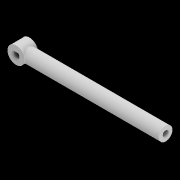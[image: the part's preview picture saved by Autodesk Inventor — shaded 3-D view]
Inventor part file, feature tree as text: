
AUTODESK INVENTOR PART (.ipt)
format: ipt  version: 2020 (Build 240168000, 168)  size: 155,648 bytes
history: native  units: mm
features: sketch x3, extrude x2, plane x1, hole x1, fillet x1, projected_geometry x1
ambient origin geometry x8: Origin, YZ Plane, XZ Plane, XY Plane, X Axis, Y Axis, Z Axis, Center Point
bodies: Solid1 (feature_tree)
feature tree (9):
  extrude  "Extrusion1"  Depth=0.5mm
  plane  "Work Plane1"
  extrude  "Extrusion2"  Depth=8.0mm
  hole  "Hole1"  [1 undecoded]
  fillet  "Fillet1"  Radius=0.5mm
  sketch  "Sketch1"  dims[d0=4.1mm d2=0.5mm]
  sketch  "Sketch2"  dims[d3=8.0mm d4=0.0mm d5=8.0mm]
  projected_geometry  "Projected Loop1"
  sketch  "Sketch3"  dims[d6=80.0mm d7=2.0mm d8=0.0mm d9=0.0mm d10=3.4mm d11=9.95mm d12=3.023mm d13=2.0mm d14=14.3117mm d15=176.2125mm d16=0.0mm d17=10.0mm d18=0.5mm]
note: 1 required parameter value undecoded (feature->parameter linkage not recoverable at this tier; creation-order binding heuristic only, values carry confidence <= 0.55)
